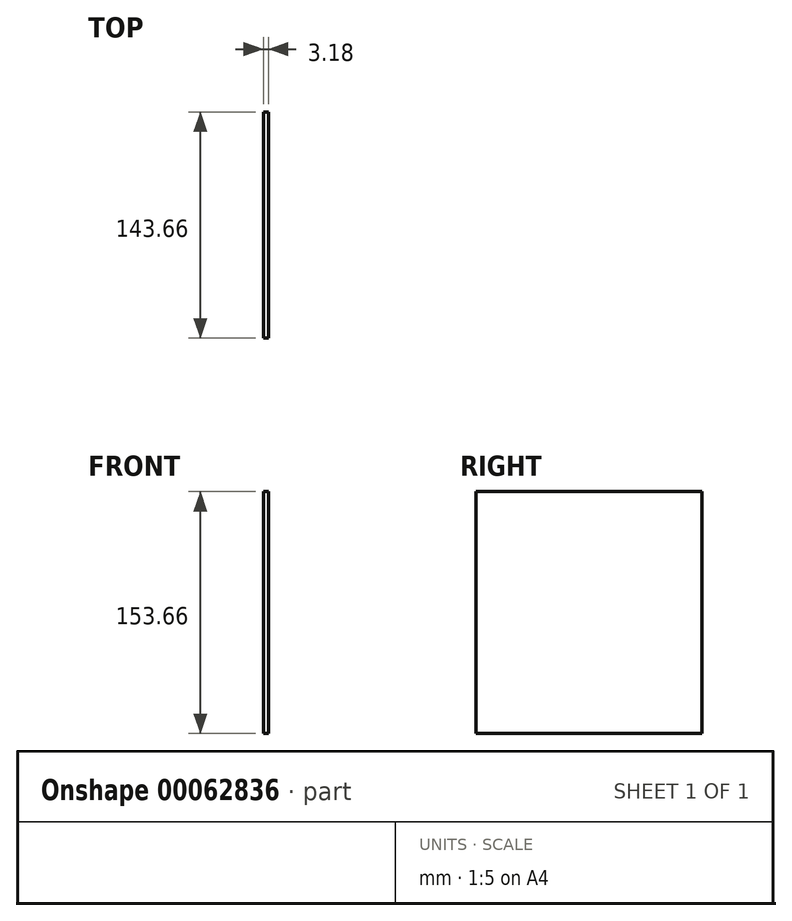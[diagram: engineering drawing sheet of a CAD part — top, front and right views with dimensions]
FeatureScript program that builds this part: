
annotation { "Feature Type Name" : "Feature", "Feature Type Description" : "" }
export const myFeature = defineFeature(function(context is Context, id is Id, definition is map)
    precondition{}
    {
        {
            var Q0;
            Q0=qCreatedBy(makeId("Right.planeOp"),FACE);
            var sketch = newSketch(context, id + "F0", { "sketchPlane" : qUnion([Q0])});
            skLineSegment(sketch, "E0.rect.bottom", {"start": v(-71.82, 76.83) * mm, "end": v(71.83, 76.83) * mm});
            skLineSegment(sketch, "E0.rect.top", {"start": v(-71.83, -76.83) * mm, "end": v(71.82, -76.83) * mm});
            skLineSegment(sketch, "E0.rect.left", {"start": v(-71.82, 76.83) * mm, "end": v(-71.83, -76.83) * mm});
            skLineSegment(sketch, "E0.rect.right", {"start": v(71.83, 76.83) * mm, "end": v(71.82, -76.83) * mm});
            skPoint(sketch, "E0.rect.middle", {"position": v(0, 0) * mm});
            skSolve(sketch);
        }
        {
            var Q0;
            Q0=makeQuery(id+"F0.imprint","IMPRINT",FACE,{"disambiguationData":[TD([[makeQuery(id+"F0.imprint","IMPRINT",EDGE,{"derivedFrom":sQuery(id+"F0.wireOp",EDGE,"E0.rect.bottom")}),-1.0]])]});
            extrude(context, id + "F1", {"entities" : qUnion([Q0]), "endBound" : BoundingType.SYMMETRIC, "depth" : 3.17 * mm});
        }
    });
